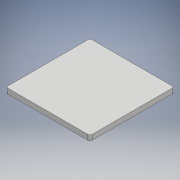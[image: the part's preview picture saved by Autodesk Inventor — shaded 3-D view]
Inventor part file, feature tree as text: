
AUTODESK INVENTOR PART (.ipt)
format: ipt  version: 2017 (Build 210142000, 142)  size: 325,120 bytes
history: native  units: mm
features: extrude x4, sketch x4, chamfer x2, fillet x1, pattern_circular x1, projected_geometry x1
ambient origin geometry x8: Origin, YZ Plane, XZ Plane, XY Plane, X Axis, Y Axis, Z Axis, Center Point
bodies: Solid1 (feature_tree)
feature tree (13):
  extrude  "Extrusion1"  Depth=80.0mm
  extrude  "Extrusion2"  Depth=1.0mm
  fillet  "Fillet1"  Radius=5.0mm
  extrude  "Extrusion3"  Depth=1.5mm TaperAngle=0.0deg
  chamfer  "Chamfer1"  Distance=1.0mm Angle=45.0deg
  chamfer  "Chamfer2"  Distance=20.0mm
  pattern_circular  "Circular Pattern1"  Count=3  [1 undecoded]
  extrude  "Extrusion4"  Depth=1.0mm TaperAngle=45.0deg
  sketch  "Sketch1"  dims[d0=80.0mm d1=80.0mm]
  sketch  "Sketch2"  dims[d2=0.3mm d3=0.0mm d4=1.0mm d5=5.0mm d6=0.0mm]
  projected_geometry  "Projected Loop1"
  sketch  "Sketch3"  dims[d7=2.0mm d8=1.5mm d9=0.0mm d10=1.0mm d11=2.0mm d12=45.0deg]
  sketch  "Sketch4"  dims[d13=3.0mm d14=20.0mm d15=30.0mm d16=1.0mm d17=2.0mm d18=45.0deg d19=40.0mm d20=40.0mm d21=30.0mm d22=180.0deg d24=0.8mm d25=1.5mm d26=0.0mm]
note: 1 required parameter value undecoded (feature->parameter linkage not recoverable at this tier; creation-order binding heuristic only, values carry confidence <= 0.55)
